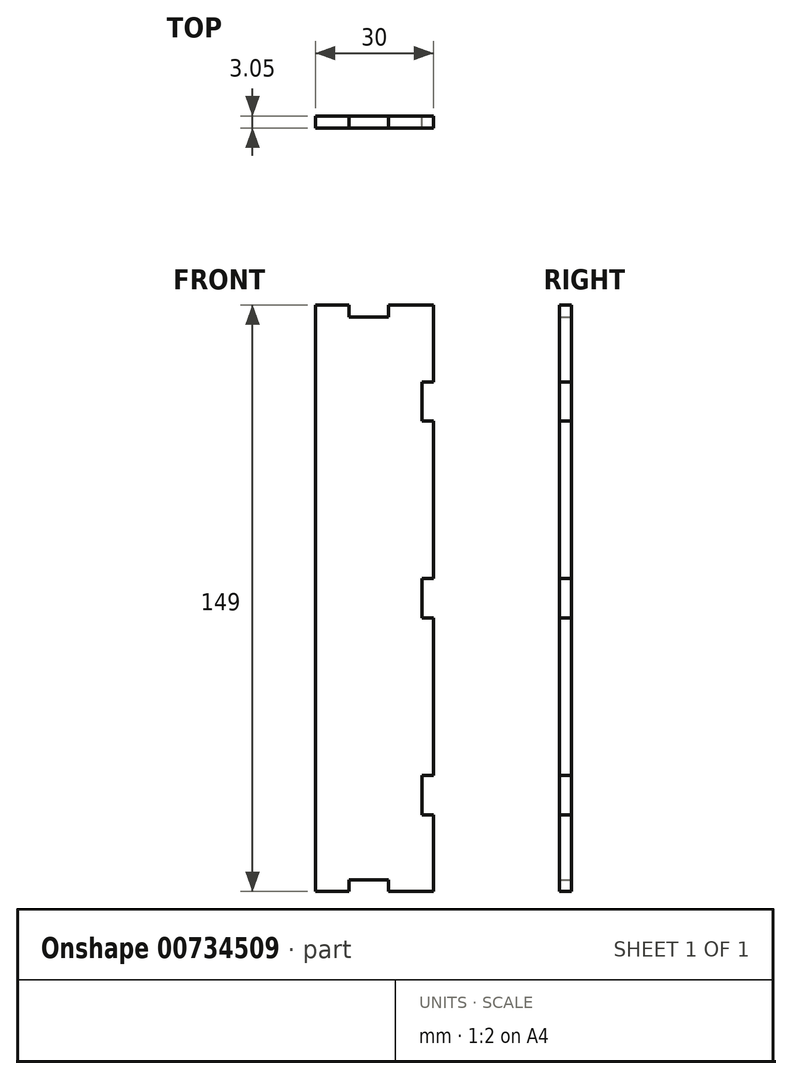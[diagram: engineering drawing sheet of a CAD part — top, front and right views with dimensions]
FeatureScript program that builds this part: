
annotation { "Feature Type Name" : "Feature", "Feature Type Description" : "" }
export const myFeature = defineFeature(function(context is Context, id is Id, definition is map)
    precondition{}
    {
        {
            var Q0;
            Q0=qCreatedBy(makeId("Front.planeOp"),FACE);
            var sketch = newSketch(context, id + "F0", { "sketchPlane" : qUnion([Q0])});
            skLineSegment(sketch, "E0", {"start": v(-6.5, -71.5) * mm, "end": v(-6.5, -74.5) * mm});
            skLineSegment(sketch, "E1", {"start": v(-6.5, -74.5) * mm, "end": v(-15, -74.5) * mm});
            skLineSegment(sketch, "E2", {"start": v(-15, -74.5) * mm, "end": v(-15, 74.5) * mm});
            skLineSegment(sketch, "E3", {"start": v(-15, 74.5) * mm, "end": v(-6.5, 74.5) * mm});
            skLineSegment(sketch, "E4", {"start": v(-6.5, 74.5) * mm, "end": v(-6.5, 71.5) * mm});
            skLineSegment(sketch, "E5", {"start": v(-6.5, 71.5) * mm, "end": v(3.5, 71.5) * mm});
            skLineSegment(sketch, "E6", {"start": v(3.5, 71.5) * mm, "end": v(3.5, 74.5) * mm});
            skLineSegment(sketch, "E7", {"start": v(3.5, 74.5) * mm, "end": v(15, 74.5) * mm});
            skLineSegment(sketch, "E8", {"start": v(15, 74.5) * mm, "end": v(15, 55) * mm});
            skLineSegment(sketch, "E9", {"start": v(15, 55) * mm, "end": v(12, 55) * mm});
            skLineSegment(sketch, "E10", {"start": v(12, 55) * mm, "end": v(12, 45) * mm});
            skLineSegment(sketch, "E11", {"start": v(12, 45) * mm, "end": v(15, 45) * mm});
            skLineSegment(sketch, "E12", {"start": v(15, 45) * mm, "end": v(15, 5) * mm});
            skLineSegment(sketch, "E13", {"start": v(15, 5) * mm, "end": v(12, 5) * mm});
            skLineSegment(sketch, "E14", {"start": v(12, 5) * mm, "end": v(12, -5) * mm});
            skLineSegment(sketch, "E15", {"start": v(12, -5) * mm, "end": v(15, -5) * mm});
            skLineSegment(sketch, "E16", {"start": v(15, -5) * mm, "end": v(15, -45) * mm});
            skLineSegment(sketch, "E17", {"start": v(15, -45) * mm, "end": v(12, -45) * mm});
            skLineSegment(sketch, "E18", {"start": v(12, -45) * mm, "end": v(12, -55) * mm});
            skLineSegment(sketch, "E19", {"start": v(12, -55) * mm, "end": v(15, -55) * mm});
            skLineSegment(sketch, "E20", {"start": v(15, -55) * mm, "end": v(15, -74.5) * mm});
            skLineSegment(sketch, "E21", {"start": v(15, -74.5) * mm, "end": v(3.5, -74.5) * mm});
            skLineSegment(sketch, "E22", {"start": v(3.5, -74.5) * mm, "end": v(3.5, -71.5) * mm});
            skLineSegment(sketch, "E23", {"start": v(3.5, -71.5) * mm, "end": v(-6.5, -71.5) * mm});
            skSolve(sketch);
        }
        {
            var Q0;
            Q0 = qSketchRegion(id + "F0", true);
            extrude(context, id + "F1", {"entities" : qUnion([Q0]), "depth" : 3.05 * mm, "offsetDistance" : 25.4 * mm});
        }
    });
